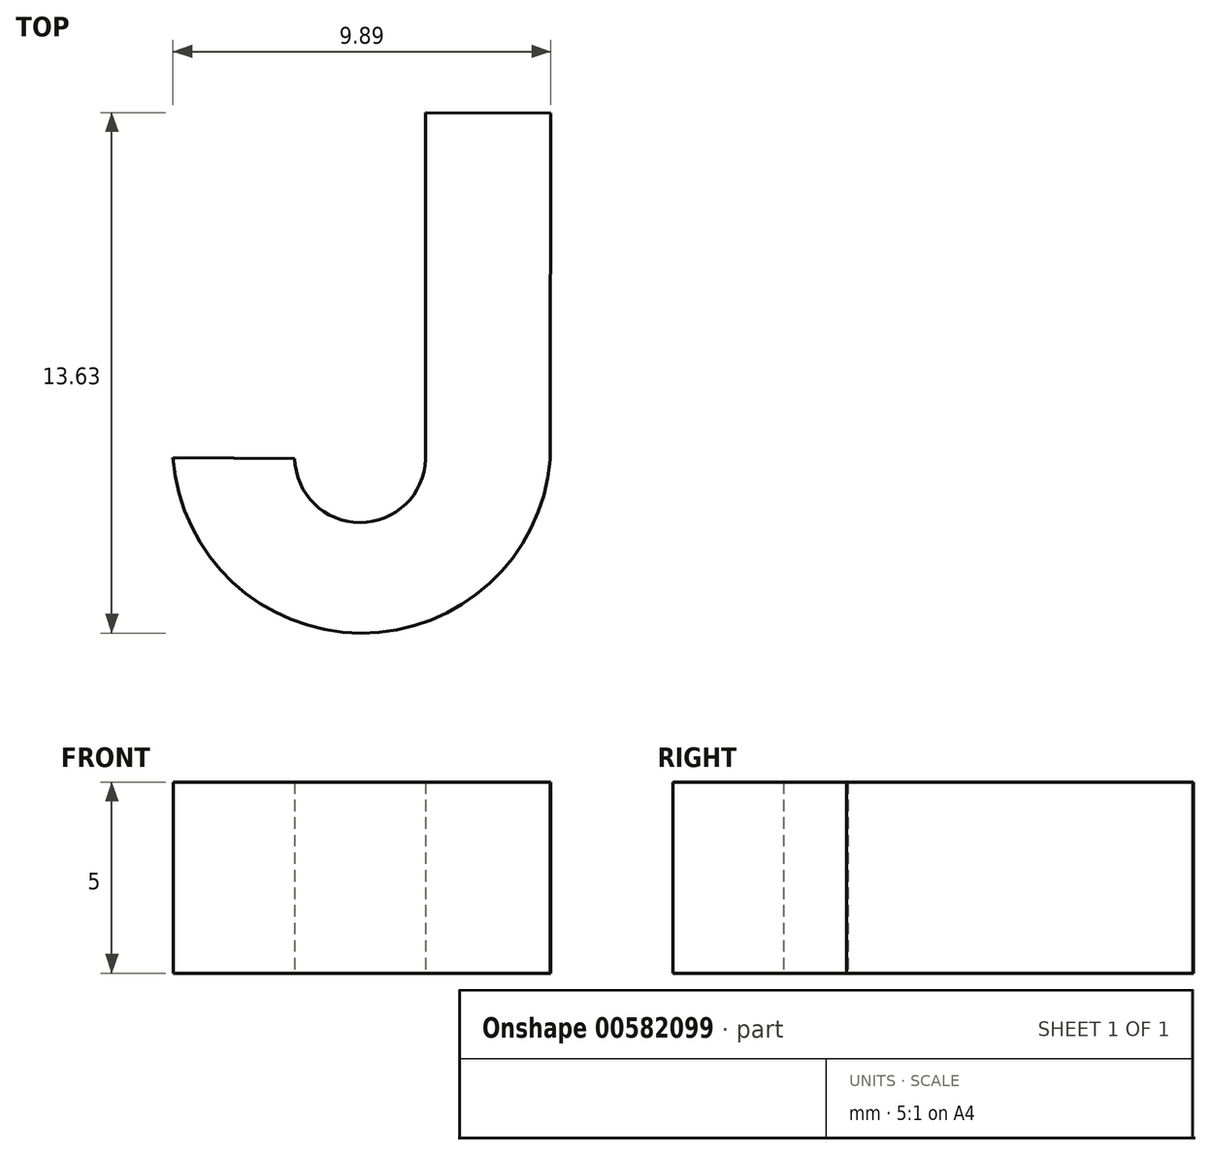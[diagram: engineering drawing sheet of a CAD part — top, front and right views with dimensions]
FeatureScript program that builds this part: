
annotation { "Feature Type Name" : "Feature", "Feature Type Description" : "" }
export const myFeature = defineFeature(function(context is Context, id is Id, definition is map)
    precondition{}
    {
        {
            var Q0;
            Q0=qCreatedBy(makeId("Top.planeOp"),FACE);
            var sketch = newSketch(context, id + "F0", { "sketchPlane" : qUnion([Q0])});
            skArc(sketch, "E0", {"start": v(-68.6, 44.33) * mm, "mid": v(-63.68, 39.74) * mm, "end": v(-58.72, 44.28) * mm});
            skLineSegment(sketch, "E1", {"start": v(-68.6, 44.33) * mm, "end": v(-65.41, 44.31) * mm});
            skArc(sketch, "E2", {"start": v(-65.41, 44.31) * mm, "mid": v(-63.7, 42.64) * mm, "end": v(-61.99, 44.3) * mm});
            skLineSegment(sketch, "E3", {"start": v(-58.72, 44.28) * mm, "end": v(-58.72, 47.18) * mm});
            skLineSegment(sketch, "E4", {"start": v(-58.72, 47.18) * mm, "end": v(-58.7, 51.1) * mm});
            skLineSegment(sketch, "E5", {"start": v(-58.7, 51.1) * mm, "end": v(-58.7, 51.1) * mm});
            skLineSegment(sketch, "E6", {"start": v(-58.7, 51.1) * mm, "end": v(-58.7, 53.35) * mm});
            skLineSegment(sketch, "E7", {"start": v(-58.7, 53.35) * mm, "end": v(-61.99, 53.37) * mm});
            skLineSegment(sketch, "E8", {"start": v(-61.99, 53.37) * mm, "end": v(-61.99, 51.1) * mm});
            skLineSegment(sketch, "E9", {"start": v(-61.99, 51.1) * mm, "end": v(-61.99, 51.1) * mm});
            skLineSegment(sketch, "E10", {"start": v(-61.99, 51.1) * mm, "end": v(-61.99, 44.3) * mm});
            skSolve(sketch);
        }
        {
            var Q0;
            Q0 = qSketchRegion(id + "F0", true);
            extrude(context, id + "F1", {"entities" : qUnion([Q0]), "depth" : 5 * mm, "offsetDistance" : 25 * mm});
        }
    });
